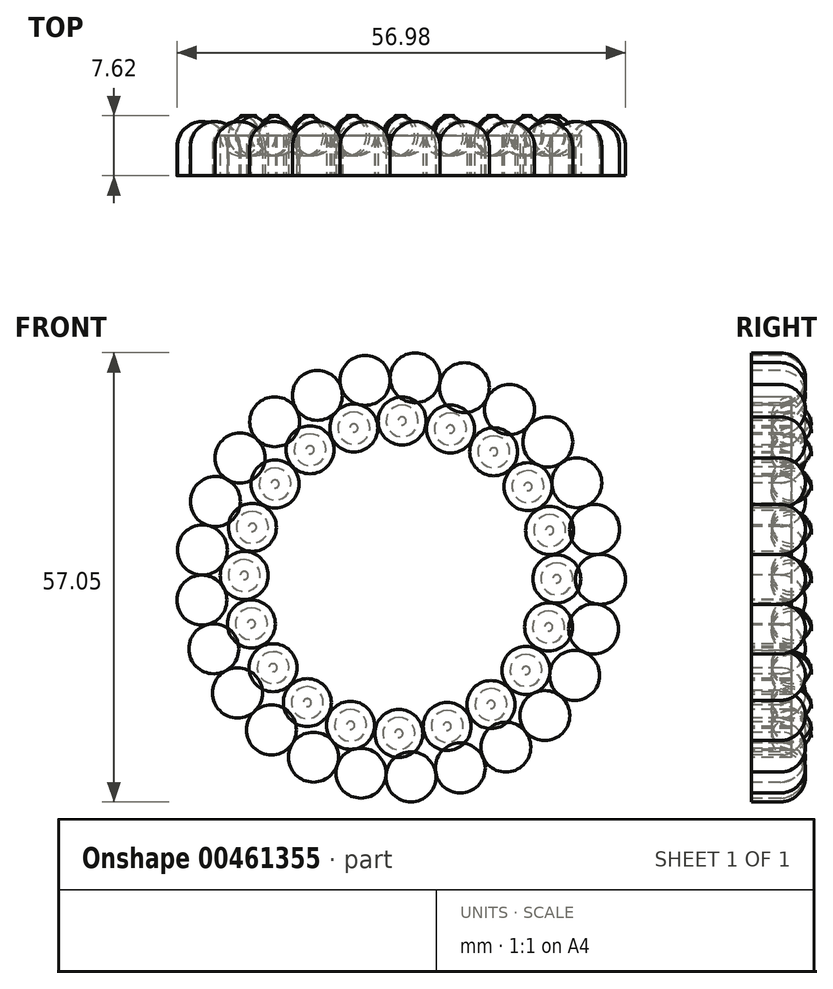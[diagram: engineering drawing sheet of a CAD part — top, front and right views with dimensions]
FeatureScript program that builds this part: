
annotation { "Feature Type Name" : "Feature", "Feature Type Description" : "" }
export const myFeature = defineFeature(function(context is Context, id is Id, definition is map)
    precondition{}
    {
        {
            var Q0;
            Q0=qCreatedBy(makeId("Front.planeOp"),FACE);
            var sketch = newSketch(context, id + "F0", { "sketchPlane" : qUnion([Q0])});
            skCircle(sketch, "E0", {"center": v(0, 0) * mm, "radius": 25.4 * mm, "construction": true});
            skCircle(sketch, "E1", {"center": v(-10.57, 23.1) * mm, "radius": 3.18 * mm});
            skSolve(sketch);
        }
        {
            var Q0;
            Q0=makeQuery(id+"F0.imprint","IMPRINT",FACE,{"disambiguationData":[TD([[makeQuery(id+"F0.imprint","IMPRINT",EDGE,{"derivedFrom":sQuery(id+"F0.wireOp",EDGE,"E1")}),1.0]])]});
            extrude(context, id + "F1", {"entities" : qUnion([Q0]), "oppositeDirection" : true, "depth" : 6.86 * mm});
        }
        {
            var Q0;
            Q0=makeQuery(id+"F1.opExtrude","SWEPT_BODY",BODY,{"disambiguationData":[OSD([sQuery(id+"F0.wireOp",EDGE,"E1")])]});
            var Q1;
            Q1=sQuery(id+"F0.wireOp",EDGE,"E0");
            circularPattern(context, id + "F2", {"entities" : qUnion([Q0]), "axis" : qUnion([Q1]), "angle" : 360 * degree, "instanceCount" : 25, "oppositeDirection" : true, "equalSpace" : true});
        }
        {
            var Q0;
            Q0=qCreatedBy(makeId("Front.planeOp"),FACE);
            var sketch = newSketch(context, id + "F3", { "sketchPlane" : qUnion([Q0])});
            skCircle(sketch, "E2", {"center": v(-5.93, 18.95) * mm, "radius": 3.05 * mm});
            skSolve(sketch);
        }
        {
            var Q0;
            Q0=makeQuery(id+"F3.imprint","IMPRINT",FACE,{"disambiguationData":[TD([[makeQuery(id+"F3.imprint","IMPRINT",EDGE,{"derivedFrom":sQuery(id+"F3.wireOp",EDGE,"E2")}),1.0]])]});
            extrude(context, id + "F4", {"entities" : qUnion([Q0]), "oppositeDirection" : true, "depth" : 7.62 * mm});
        }
        {
            var Q0;
            Q0=makeQuery(id+"F4.opExtrude","SWEPT_BODY",BODY,{"disambiguationData":[OSD([sQuery(id+"F3.wireOp",EDGE,"E2")])]});
            var Q1;
            Q1=sQuery(id+"F0.wireOp",EDGE,"E0");
            circularPattern(context, id + "F5", {"entities" : qUnion([Q0]), "axis" : qUnion([Q1]), "angle" : 360 * degree, "instanceCount" : 20, "equalSpace" : true});
        }
        {
            var Q0;
            Q0=makeQuery(id+"F2.opPattern","COPY",FACE,{"derivedFrom":makeQuery(id+"F1.opExtrude","CAP_FACE",FACE,{"disambiguationData":[OSD([sQuery(id+"F0.wireOp",EDGE,"E1")])],"isStart":false}),"instanceName":"11"});
            var Q1;
            Q1=makeQuery(id+"F2.opPattern","COPY",FACE,{"derivedFrom":makeQuery(id+"F1.opExtrude","CAP_FACE",FACE,{"disambiguationData":[OSD([sQuery(id+"F0.wireOp",EDGE,"E1")])],"isStart":false}),"instanceName":"10"});
            var Q2;
            Q2=makeQuery(id+"F2.opPattern","COPY",FACE,{"derivedFrom":makeQuery(id+"F1.opExtrude","CAP_FACE",FACE,{"disambiguationData":[OSD([sQuery(id+"F0.wireOp",EDGE,"E1")])],"isStart":false}),"instanceName":"9"});
            var Q3;
            Q3=makeQuery(id+"F2.opPattern","COPY",FACE,{"derivedFrom":makeQuery(id+"F1.opExtrude","CAP_FACE",FACE,{"disambiguationData":[OSD([sQuery(id+"F0.wireOp",EDGE,"E1")])],"isStart":false}),"instanceName":"6"});
            var Q4;
            Q4=makeQuery(id+"F2.opPattern","COPY",FACE,{"derivedFrom":makeQuery(id+"F1.opExtrude","CAP_FACE",FACE,{"disambiguationData":[OSD([sQuery(id+"F0.wireOp",EDGE,"E1")])],"isStart":false}),"instanceName":"13"});
            var Q5;
            Q5=makeQuery(id+"F2.opPattern","COPY",EDGE,{"derivedFrom":makeQuery(id+"F1.opExtrude","CAP_EDGE",EDGE,{"disambiguationData":[OSD([sQuery(id+"F0.wireOp",EDGE,"E1")])],"isStart":false}),"instanceName":"12"});
            var Q6;
            Q6=makeQuery(id+"F2.opPattern","COPY",EDGE,{"derivedFrom":makeQuery(id+"F1.opExtrude","CAP_EDGE",EDGE,{"disambiguationData":[OSD([sQuery(id+"F0.wireOp",EDGE,"E1")])],"isStart":false}),"instanceName":"14"});
            var Q7;
            Q7=makeQuery(id+"F2.opPattern","COPY",EDGE,{"derivedFrom":makeQuery(id+"F1.opExtrude","CAP_EDGE",EDGE,{"disambiguationData":[OSD([sQuery(id+"F0.wireOp",EDGE,"E1")])],"isStart":false}),"instanceName":"15"});
            var Q8;
            Q8=makeQuery(id+"F2.opPattern","COPY",EDGE,{"derivedFrom":makeQuery(id+"F1.opExtrude","CAP_EDGE",EDGE,{"disambiguationData":[OSD([sQuery(id+"F0.wireOp",EDGE,"E1")])],"isStart":false}),"instanceName":"16"});
            var Q9;
            Q9=makeQuery(id+"F2.opPattern","COPY",EDGE,{"derivedFrom":makeQuery(id+"F1.opExtrude","CAP_EDGE",EDGE,{"disambiguationData":[OSD([sQuery(id+"F0.wireOp",EDGE,"E1")])],"isStart":false}),"instanceName":"17"});
            var Q10;
            Q10=makeQuery(id+"F2.opPattern","COPY",EDGE,{"derivedFrom":makeQuery(id+"F1.opExtrude","CAP_EDGE",EDGE,{"disambiguationData":[OSD([sQuery(id+"F0.wireOp",EDGE,"E1")])],"isStart":false}),"instanceName":"18"});
            var Q11;
            Q11=makeQuery(id+"F2.opPattern","COPY",EDGE,{"derivedFrom":makeQuery(id+"F1.opExtrude","CAP_EDGE",EDGE,{"disambiguationData":[OSD([sQuery(id+"F0.wireOp",EDGE,"E1")])],"isStart":false}),"instanceName":"19"});
            var Q12;
            Q12=makeQuery(id+"F2.opPattern","COPY",EDGE,{"derivedFrom":makeQuery(id+"F1.opExtrude","CAP_EDGE",EDGE,{"disambiguationData":[OSD([sQuery(id+"F0.wireOp",EDGE,"E1")])],"isStart":false}),"instanceName":"20"});
            var Q13;
            Q13=makeQuery(id+"F2.opPattern","COPY",EDGE,{"derivedFrom":makeQuery(id+"F1.opExtrude","CAP_EDGE",EDGE,{"disambiguationData":[OSD([sQuery(id+"F0.wireOp",EDGE,"E1")])],"isStart":false}),"instanceName":"21"});
            var Q14;
            Q14=makeQuery(id+"F2.opPattern","COPY",EDGE,{"derivedFrom":makeQuery(id+"F1.opExtrude","CAP_EDGE",EDGE,{"disambiguationData":[OSD([sQuery(id+"F0.wireOp",EDGE,"E1")])],"isStart":false}),"instanceName":"22"});
            var Q15;
            Q15=makeQuery(id+"F2.opPattern","COPY",EDGE,{"derivedFrom":makeQuery(id+"F1.opExtrude","CAP_EDGE",EDGE,{"disambiguationData":[OSD([sQuery(id+"F0.wireOp",EDGE,"E1")])],"isStart":false}),"instanceName":"8"});
            var Q16;
            Q16=makeQuery(id+"F2.opPattern","COPY",EDGE,{"derivedFrom":makeQuery(id+"F1.opExtrude","CAP_EDGE",EDGE,{"disambiguationData":[OSD([sQuery(id+"F0.wireOp",EDGE,"E1")])],"isStart":false}),"instanceName":"7"});
            var Q17;
            Q17=makeQuery(id+"F2.opPattern","COPY",EDGE,{"derivedFrom":makeQuery(id+"F1.opExtrude","CAP_EDGE",EDGE,{"disambiguationData":[OSD([sQuery(id+"F0.wireOp",EDGE,"E1")])],"isStart":false}),"instanceName":"5"});
            var Q18;
            Q18=makeQuery(id+"F2.opPattern","COPY",EDGE,{"derivedFrom":makeQuery(id+"F1.opExtrude","CAP_EDGE",EDGE,{"disambiguationData":[OSD([sQuery(id+"F0.wireOp",EDGE,"E1")])],"isStart":false}),"instanceName":"4"});
            var Q19;
            Q19=makeQuery(id+"F2.opPattern","COPY",EDGE,{"derivedFrom":makeQuery(id+"F1.opExtrude","CAP_EDGE",EDGE,{"disambiguationData":[OSD([sQuery(id+"F0.wireOp",EDGE,"E1")])],"isStart":false}),"instanceName":"3"});
            var Q20;
            Q20=makeQuery(id+"F2.opPattern","COPY",EDGE,{"derivedFrom":makeQuery(id+"F1.opExtrude","CAP_EDGE",EDGE,{"disambiguationData":[OSD([sQuery(id+"F0.wireOp",EDGE,"E1")])],"isStart":false}),"instanceName":"2"});
            var Q21;
            Q21=makeQuery(id+"F2.opPattern","COPY",EDGE,{"derivedFrom":makeQuery(id+"F1.opExtrude","CAP_EDGE",EDGE,{"disambiguationData":[OSD([sQuery(id+"F0.wireOp",EDGE,"E1")])],"isStart":false}),"instanceName":"1"});
            var Q22;
            Q22=makeQuery(id+"F1.opExtrude","CAP_EDGE",EDGE,{"disambiguationData":[OSD([sQuery(id+"F0.wireOp",EDGE,"E1")])],"isStart":false});
            var Q23;
            Q23=makeQuery(id+"F2.opPattern","COPY",EDGE,{"derivedFrom":makeQuery(id+"F1.opExtrude","CAP_EDGE",EDGE,{"disambiguationData":[OSD([sQuery(id+"F0.wireOp",EDGE,"E1")])],"isStart":false}),"instanceName":"24"});
            var Q24;
            Q24=makeQuery(id+"F2.opPattern","COPY",EDGE,{"derivedFrom":makeQuery(id+"F1.opExtrude","CAP_EDGE",EDGE,{"disambiguationData":[OSD([sQuery(id+"F0.wireOp",EDGE,"E1")])],"isStart":false}),"instanceName":"23"});
            fillet(context, id + "F6", {"entities" : qUnion([Q0, Q1, Q2, Q3, Q4, Q5, Q6, Q7, Q8, Q9, Q10, Q11, Q12, Q13, Q14, Q15, Q16, Q17, Q18, Q19, Q20, Q21, Q22, Q23, Q24]), "radius" : 3.17 * mm, "tangentPropagation" : true, "allowEdgeOverflow" : false});
        }
        {
            var Q0;
            Q0=makeQuery(id+"F5.opPattern","COPY",EDGE,{"derivedFrom":makeQuery(id+"F4.opExtrude","CAP_EDGE",EDGE,{"disambiguationData":[OSD([sQuery(id+"F3.wireOp",EDGE,"E2")])],"isStart":false}),"instanceName":"15"});
            var Q1;
            Q1=makeQuery(id+"F5.opPattern","COPY",EDGE,{"derivedFrom":makeQuery(id+"F4.opExtrude","CAP_EDGE",EDGE,{"disambiguationData":[OSD([sQuery(id+"F3.wireOp",EDGE,"E2")])],"isStart":false}),"instanceName":"11"});
            var Q2;
            Q2=makeQuery(id+"F5.opPattern","COPY",EDGE,{"derivedFrom":makeQuery(id+"F4.opExtrude","CAP_EDGE",EDGE,{"disambiguationData":[OSD([sQuery(id+"F3.wireOp",EDGE,"E2")])],"isStart":false}),"instanceName":"14"});
            var Q3;
            Q3=makeQuery(id+"F5.opPattern","COPY",EDGE,{"derivedFrom":makeQuery(id+"F4.opExtrude","CAP_EDGE",EDGE,{"disambiguationData":[OSD([sQuery(id+"F3.wireOp",EDGE,"E2")])],"isStart":false}),"instanceName":"13"});
            var Q4;
            Q4=makeQuery(id+"F5.opPattern","COPY",EDGE,{"derivedFrom":makeQuery(id+"F4.opExtrude","CAP_EDGE",EDGE,{"disambiguationData":[OSD([sQuery(id+"F3.wireOp",EDGE,"E2")])],"isStart":false}),"instanceName":"12"});
            var Q5;
            Q5=makeQuery(id+"F5.opPattern","COPY",EDGE,{"derivedFrom":makeQuery(id+"F4.opExtrude","CAP_EDGE",EDGE,{"disambiguationData":[OSD([sQuery(id+"F3.wireOp",EDGE,"E2")])],"isStart":false}),"instanceName":"10"});
            var Q6;
            Q6=makeQuery(id+"F5.opPattern","COPY",EDGE,{"derivedFrom":makeQuery(id+"F4.opExtrude","CAP_EDGE",EDGE,{"disambiguationData":[OSD([sQuery(id+"F3.wireOp",EDGE,"E2")])],"isStart":false}),"instanceName":"9"});
            var Q7;
            Q7=makeQuery(id+"F5.opPattern","COPY",EDGE,{"derivedFrom":makeQuery(id+"F4.opExtrude","CAP_EDGE",EDGE,{"disambiguationData":[OSD([sQuery(id+"F3.wireOp",EDGE,"E2")])],"isStart":false}),"instanceName":"8"});
            var Q8;
            Q8=makeQuery(id+"F5.opPattern","COPY",EDGE,{"derivedFrom":makeQuery(id+"F4.opExtrude","CAP_EDGE",EDGE,{"disambiguationData":[OSD([sQuery(id+"F3.wireOp",EDGE,"E2")])],"isStart":false}),"instanceName":"7"});
            var Q9;
            Q9=makeQuery(id+"F5.opPattern","COPY",EDGE,{"derivedFrom":makeQuery(id+"F4.opExtrude","CAP_EDGE",EDGE,{"disambiguationData":[OSD([sQuery(id+"F3.wireOp",EDGE,"E2")])],"isStart":false}),"instanceName":"6"});
            var Q10;
            Q10=makeQuery(id+"F5.opPattern","COPY",EDGE,{"derivedFrom":makeQuery(id+"F4.opExtrude","CAP_EDGE",EDGE,{"disambiguationData":[OSD([sQuery(id+"F3.wireOp",EDGE,"E2")])],"isStart":false}),"instanceName":"5"});
            var Q11;
            Q11=makeQuery(id+"F5.opPattern","COPY",EDGE,{"derivedFrom":makeQuery(id+"F4.opExtrude","CAP_EDGE",EDGE,{"disambiguationData":[OSD([sQuery(id+"F3.wireOp",EDGE,"E2")])],"isStart":false}),"instanceName":"4"});
            var Q12;
            Q12=makeQuery(id+"F5.opPattern","COPY",EDGE,{"derivedFrom":makeQuery(id+"F4.opExtrude","CAP_EDGE",EDGE,{"disambiguationData":[OSD([sQuery(id+"F3.wireOp",EDGE,"E2")])],"isStart":false}),"instanceName":"3"});
            var Q13;
            Q13=makeQuery(id+"F5.opPattern","COPY",EDGE,{"derivedFrom":makeQuery(id+"F4.opExtrude","CAP_EDGE",EDGE,{"disambiguationData":[OSD([sQuery(id+"F3.wireOp",EDGE,"E2")])],"isStart":false}),"instanceName":"2"});
            var Q14;
            Q14=makeQuery(id+"F5.opPattern","COPY",EDGE,{"derivedFrom":makeQuery(id+"F4.opExtrude","CAP_EDGE",EDGE,{"disambiguationData":[OSD([sQuery(id+"F3.wireOp",EDGE,"E2")])],"isStart":false}),"instanceName":"1"});
            var Q15;
            Q15=makeQuery(id+"F4.opExtrude","CAP_EDGE",EDGE,{"disambiguationData":[OSD([sQuery(id+"F3.wireOp",EDGE,"E2")])],"isStart":false});
            var Q16;
            Q16=makeQuery(id+"F5.opPattern","COPY",EDGE,{"derivedFrom":makeQuery(id+"F4.opExtrude","CAP_EDGE",EDGE,{"disambiguationData":[OSD([sQuery(id+"F3.wireOp",EDGE,"E2")])],"isStart":false}),"instanceName":"19"});
            var Q17;
            Q17=makeQuery(id+"F5.opPattern","COPY",EDGE,{"derivedFrom":makeQuery(id+"F4.opExtrude","CAP_EDGE",EDGE,{"disambiguationData":[OSD([sQuery(id+"F3.wireOp",EDGE,"E2")])],"isStart":false}),"instanceName":"18"});
            var Q18;
            Q18=makeQuery(id+"F5.opPattern","COPY",EDGE,{"derivedFrom":makeQuery(id+"F4.opExtrude","CAP_EDGE",EDGE,{"disambiguationData":[OSD([sQuery(id+"F3.wireOp",EDGE,"E2")])],"isStart":false}),"instanceName":"17"});
            var Q19;
            Q19=makeQuery(id+"F5.opPattern","COPY",EDGE,{"derivedFrom":makeQuery(id+"F4.opExtrude","CAP_EDGE",EDGE,{"disambiguationData":[OSD([sQuery(id+"F3.wireOp",EDGE,"E2")])],"isStart":false}),"instanceName":"16"});
            fillet(context, id + "F7", {"entities" : qUnion([Q0, Q1, Q2, Q3, Q4, Q5, Q6, Q7, Q8, Q9, Q10, Q11, Q12, Q13, Q14, Q15, Q16, Q17, Q18, Q19]), "radius" : 2.54 * mm, "tangentPropagation" : true, "allowEdgeOverflow" : false});
        }
    });
